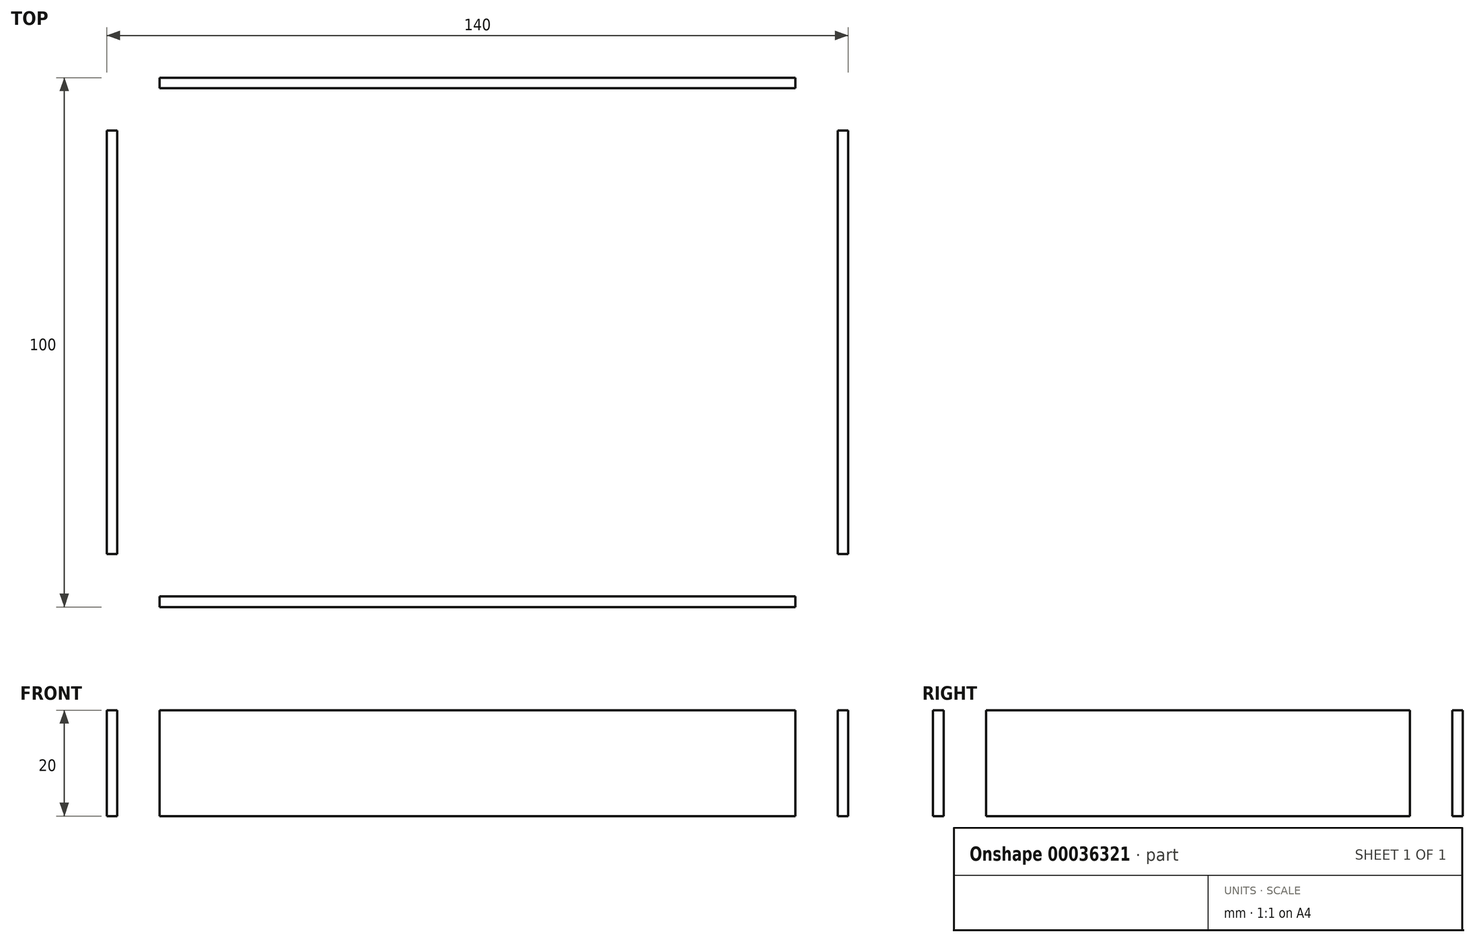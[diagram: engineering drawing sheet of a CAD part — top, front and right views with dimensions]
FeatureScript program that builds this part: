
annotation { "Feature Type Name" : "Feature", "Feature Type Description" : "" }
export const myFeature = defineFeature(function(context is Context, id is Id, definition is map)
    precondition{}
    {
        {
            var Q0;
            Q0=qCreatedBy(makeId("Top.planeOp"),FACE);
            var sketch = newSketch(context, id + "F0", { "sketchPlane" : qUnion([Q0])});
            skLineSegment(sketch, "E0.bottom", {"start": v(-69.46, 45.69) * mm, "end": v(70.54, 45.69) * mm});
            skLineSegment(sketch, "E0.top", {"start": v(-69.46, -54.31) * mm, "end": v(70.54, -54.31) * mm});
            skLineSegment(sketch, "E0.left", {"start": v(-69.46, 45.69) * mm, "end": v(-69.46, -54.31) * mm});
            skLineSegment(sketch, "E0.right", {"start": v(70.54, 45.69) * mm, "end": v(70.54, -54.31) * mm});
            skLineSegment(sketch, "E1.bottom", {"start": v(-69.46, 45.69) * mm, "end": v(-59.46, 45.69) * mm});
            skLineSegment(sketch, "E1.top", {"start": v(-69.46, 35.69) * mm, "end": v(-59.46, 35.69) * mm});
            skLineSegment(sketch, "E1.left", {"start": v(-69.46, 45.69) * mm, "end": v(-69.46, 35.69) * mm});
            skLineSegment(sketch, "E1.right", {"start": v(-59.46, 45.69) * mm, "end": v(-59.46, 35.69) * mm});
            skLineSegment(sketch, "E2.bottom", {"start": v(-69.46, -54.31) * mm, "end": v(-59.46, -54.31) * mm});
            skLineSegment(sketch, "E2.top", {"start": v(-69.46, -44.31) * mm, "end": v(-59.46, -44.31) * mm});
            skLineSegment(sketch, "E2.left", {"start": v(-69.46, -54.31) * mm, "end": v(-69.46, -44.31) * mm});
            skLineSegment(sketch, "E2.right", {"start": v(-59.46, -54.31) * mm, "end": v(-59.46, -44.31) * mm});
            skLineSegment(sketch, "E3.bottom", {"start": v(70.54, -54.31) * mm, "end": v(60.54, -54.31) * mm});
            skLineSegment(sketch, "E3.top", {"start": v(70.54, -44.31) * mm, "end": v(60.54, -44.31) * mm});
            skLineSegment(sketch, "E3.left", {"start": v(70.54, -54.31) * mm, "end": v(70.54, -44.31) * mm});
            skLineSegment(sketch, "E3.right", {"start": v(60.54, -54.31) * mm, "end": v(60.54, -44.31) * mm});
            skLineSegment(sketch, "E4.bottom", {"start": v(70.54, 45.69) * mm, "end": v(60.54, 45.69) * mm});
            skLineSegment(sketch, "E4.top", {"start": v(70.54, 35.69) * mm, "end": v(60.54, 35.69) * mm});
            skLineSegment(sketch, "E4.left", {"start": v(70.54, 45.69) * mm, "end": v(70.54, 35.69) * mm});
            skLineSegment(sketch, "E4.right", {"start": v(60.54, 45.69) * mm, "end": v(60.54, 35.69) * mm});
            skLineSegment(sketch, "E5", {"start": v(-59.46, 43.69) * mm, "end": v(60.54, 43.69) * mm});
            skLineSegment(sketch, "E6", {"start": v(-59.46, -52.31) * mm, "end": v(60.54, -52.31) * mm});
            skLineSegment(sketch, "E7", {"start": v(-67.46, 35.69) * mm, "end": v(-67.46, -44.31) * mm});
            skLineSegment(sketch, "E8", {"start": v(68.54, -44.31) * mm, "end": v(68.54, 35.69) * mm});
            skLineSegment(sketch, "E9", {"start": v(-69.46, -4.31) * mm, "end": v(-67.46, -4.31) * mm});
            skLineSegment(sketch, "E10", {"start": v(0, -52.31) * mm, "end": v(0, -54.31) * mm, "construction": true});
            skLineSegment(sketch, "E11", {"start": v(70.54, -4.31) * mm, "end": v(68.54, -4.31) * mm, "construction": true});
            skLineSegment(sketch, "E12", {"start": v(0.54, 45.69) * mm, "end": v(0.54, 43.69) * mm, "construction": true});
            skCircle(sketch, "E13", {"center": v(-64.46, 40.69) * mm, "radius": 1.5 * mm});
            skCircle(sketch, "E14", {"center": v(-64.46, -49.31) * mm, "radius": 1.5 * mm});
            skCircle(sketch, "E15", {"center": v(65.54, 40.69) * mm, "radius": 1.5 * mm});
            skCircle(sketch, "E16", {"center": v(65.54, -49.31) * mm, "radius": 1.5 * mm});
            skLineSegment(sketch, "E17", {"start": v(-64.46, 35.69) * mm, "end": v(-64.46, 45.69) * mm, "construction": true});
            skLineSegment(sketch, "E18", {"start": v(-59.46, 40.69) * mm, "end": v(-64.46, 40.69) * mm, "construction": true});
            skLineSegment(sketch, "E19", {"start": v(-64.46, 40.69) * mm, "end": v(-69.46, 40.69) * mm, "construction": true});
            skLineSegment(sketch, "E20", {"start": v(65.54, -44.31) * mm, "end": v(65.54, -54.31) * mm, "construction": true});
            skLineSegment(sketch, "E21", {"start": v(60.54, -49.31) * mm, "end": v(65.54, -49.31) * mm, "construction": true});
            skLineSegment(sketch, "E22", {"start": v(65.54, -49.31) * mm, "end": v(70.54, -49.31) * mm, "construction": true});
            skSolve(sketch);
        }
        {
            var Q0;
            {var subQ2=sQuery(id+"F0.wireOp",EDGE,"E0.right");Q0=makeQuery(id+"F0.imprint","IMPRINT",FACE,{"disambiguationData":[TD([[makeQuery(id+"F0.imprint","IMPRINT",EDGE,{"derivedFrom":subQ2}),-1.0]])]});}
            var Q1;
            {var subQ4=sQuery(id+"F0.wireOp",EDGE,"E3.bottom");Q1=makeQuery(id+"F0.imprint","IMPRINT",FACE,{"disambiguationData":[TD([[makeQuery(id+"F0.imprint","IMPRINT",EDGE,{"derivedFrom":subQ4}),-1.0]])]});}
            var Q2;
            {var subQ2=sQuery(id+"F0.wireOp",EDGE,"E0.top");Q2=makeQuery(id+"F0.imprint","IMPRINT",FACE,{"disambiguationData":[TD([[makeQuery(id+"F0.imprint","IMPRINT",EDGE,{"derivedFrom":subQ2}),1.0]])]});}
            var Q3;
            {var subQ0=sQuery(id+"F0.wireOp",EDGE,"E9");Q3=makeQuery(id+"F0.imprint","IMPRINT",FACE,{"disambiguationData":[TD([[makeQuery(id+"F0.imprint","IMPRINT",EDGE,{"derivedFrom":subQ0}),-1.0]])]});}
            var Q4;
            {var subQ4=sQuery(id+"F0.wireOp",EDGE,"E2.bottom");Q4=makeQuery(id+"F0.imprint","IMPRINT",FACE,{"disambiguationData":[TD([[makeQuery(id+"F0.imprint","IMPRINT",EDGE,{"derivedFrom":subQ4}),1.0]])]});}
            var Q5;
            {var subQ0=sQuery(id+"F0.wireOp",EDGE,"E9");Q5=makeQuery(id+"F0.imprint","IMPRINT",FACE,{"disambiguationData":[TD([[makeQuery(id+"F0.imprint","IMPRINT",EDGE,{"derivedFrom":subQ0}),1.0]])]});}
            var Q6;
            {var subQ4=sQuery(id+"F0.wireOp",EDGE,"E1.bottom");Q6=makeQuery(id+"F0.imprint","IMPRINT",FACE,{"disambiguationData":[TD([[makeQuery(id+"F0.imprint","IMPRINT",EDGE,{"derivedFrom":subQ4}),-1.0]])]});}
            var Q7;
            {var subQ2=sQuery(id+"F0.wireOp",EDGE,"E0.bottom");Q7=makeQuery(id+"F0.imprint","IMPRINT",FACE,{"disambiguationData":[TD([[makeQuery(id+"F0.imprint","IMPRINT",EDGE,{"derivedFrom":subQ2}),-1.0]])]});}
            var Q8;
            {var subQ4=sQuery(id+"F0.wireOp",EDGE,"E4.bottom");Q8=makeQuery(id+"F0.imprint","IMPRINT",FACE,{"disambiguationData":[TD([[makeQuery(id+"F0.imprint","IMPRINT",EDGE,{"derivedFrom":subQ4}),1.0]])]});}
            extrude(context, id + "F1", {"entities" : qUnion([Q0, Q1, Q2, Q3, Q4, Q5, Q6, Q7, Q8]), "depth" : 20 * mm});
        }
    });
